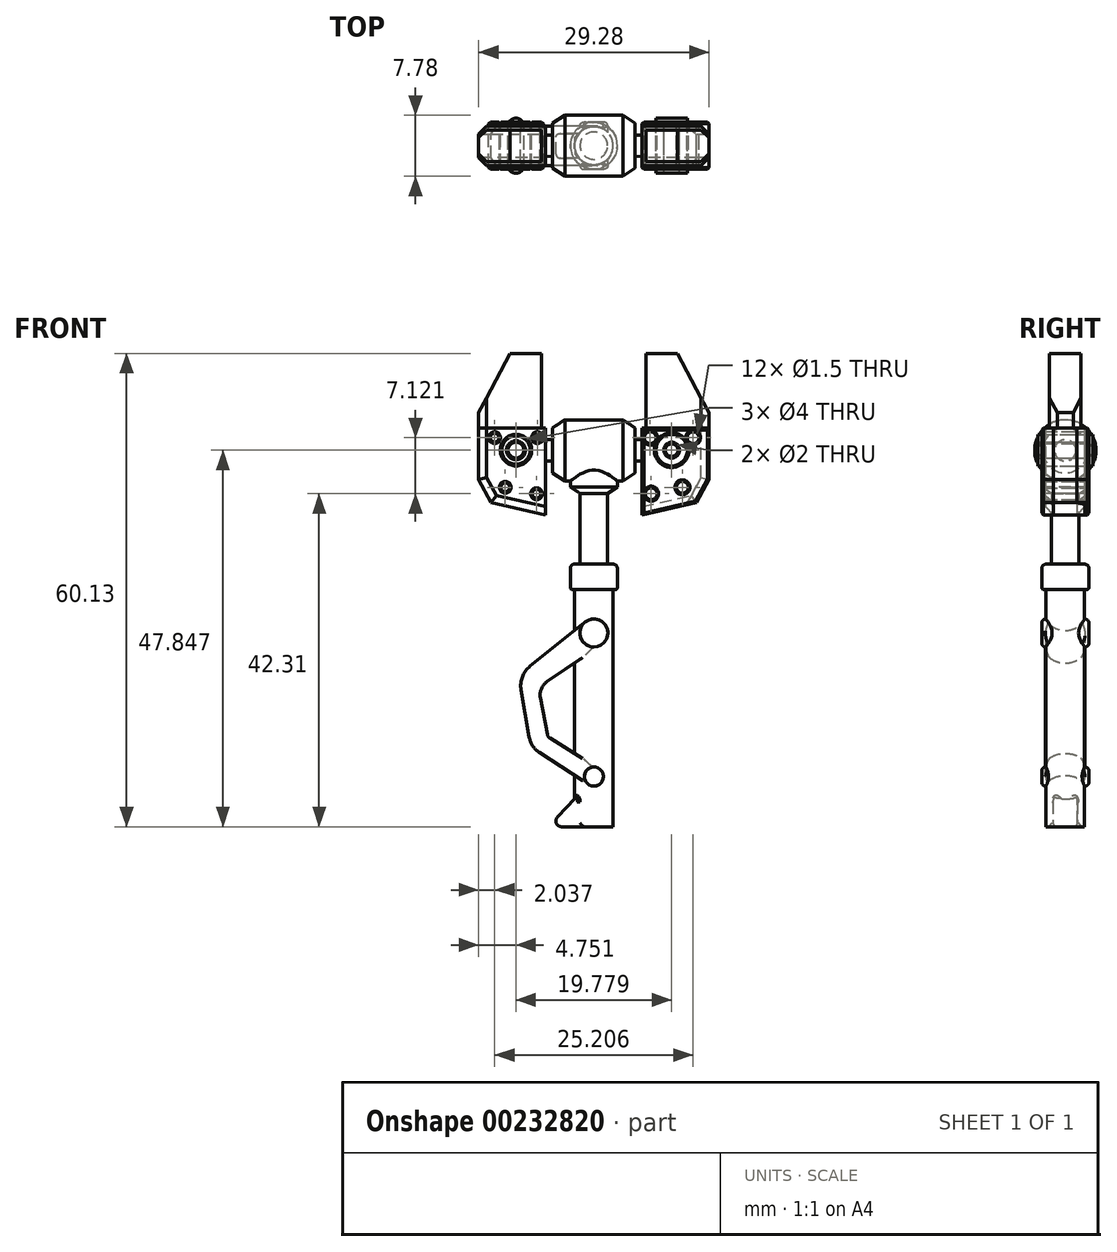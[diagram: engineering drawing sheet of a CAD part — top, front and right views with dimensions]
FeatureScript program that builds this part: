
annotation { "Feature Type Name" : "Feature", "Feature Type Description" : "" }
export const myFeature = defineFeature(function(context is Context, id is Id, definition is map)
    precondition{}
    {
        {
            var Q0;
            Q0=qCreatedBy(makeId("Front.planeOp"),FACE);
            var sketch = newSketch(context, id + "F0", { "sketchPlane" : qUnion([Q0])});
            skLineSegment(sketch, "E0", {"start": v(0, -35.9) * mm, "end": v(0, 32.83) * mm, "construction": true});
            skSolve(sketch);
        }
        {
            var Q0;
            Q0=qCreatedBy(makeId("Front.planeOp"),FACE);
            var sketch = newSketch(context, id + "F1", { "sketchPlane" : qUnion([Q0])});
            skLineSegment(sketch, "E1", {"start": v(-6.64, 28.64) * mm, "end": v(-10.64, 28.64) * mm});
            skLineSegment(sketch, "E2", {"start": v(-10.64, 28.64) * mm, "end": v(-14.64, 21.12) * mm});
            skLineSegment(sketch, "E3", {"start": v(-14.64, 21.12) * mm, "end": v(-14.64, 12.62) * mm});
            skLineSegment(sketch, "E4", {"start": v(-14.64, 12.62) * mm, "end": v(-13.04, 9.73) * mm});
            skLineSegment(sketch, "E5", {"start": v(-13.04, 9.73) * mm, "end": v(-6.14, 8.14) * mm});
            skLineSegment(sketch, "E6", {"start": v(-6.14, 8.14) * mm, "end": v(-6.14, 19.14) * mm});
            skLineSegment(sketch, "E7", {"start": v(-6.14, 19.14) * mm, "end": v(-6.64, 19.14) * mm});
            skLineSegment(sketch, "E8", {"start": v(-6.64, 19.14) * mm, "end": v(-6.64, 28.64) * mm});
            skLineSegment(sketch, "E9", {"start": v(-6.64, 19.14) * mm, "end": v(-14.64, 19.14) * mm});
            skCircle(sketch, "E10", {"center": v(-9.89, 16.36) * mm, "radius": 1 * mm});
            skCircle(sketch, "E11.0", {"center": v(-9.89, 16.36) * mm, "radius": 2 * mm});
            skCircle(sketch, "E12", {"center": v(-11.25, 11.63) * mm, "radius": 0.75 * mm});
            skCircle(sketch, "E13", {"center": v(-7.28, 10.82) * mm, "radius": 0.75 * mm});
            skCircle(sketch, "E14", {"center": v(-7.16, 17.94) * mm, "radius": 0.75 * mm});
            skLineSegment(sketch, "E15", {"start": v(-6.14, 17.67) * mm, "end": v(-5.23, 17.68) * mm});
            skLineSegment(sketch, "E16", {"start": v(-5.23, 17.68) * mm, "end": v(-5.25, 19.18) * mm});
            skLineSegment(sketch, "E17", {"start": v(-5.25, 19.18) * mm, "end": v(-3.69, 20.2) * mm});
            skLineSegment(sketch, "E18", {"start": v(-6.14, 16.32) * mm, "end": v(0, 16.32) * mm});
            skLineSegment(sketch, "E19.MirrorCS", {"start": v(6.14, 16.32) * mm, "end": v(0, 16.32) * mm});
            skLineSegment(sketch, "E20.MirrorCS", {"start": v(6.64, 19.14) * mm, "end": v(6.64, 28.64) * mm});
            skLineSegment(sketch, "E21.MirrorCS", {"start": v(6.64, 28.64) * mm, "end": v(10.64, 28.64) * mm});
            skLineSegment(sketch, "E22.MirrorCS", {"start": v(10.64, 28.64) * mm, "end": v(14.64, 21.12) * mm});
            skLineSegment(sketch, "E23.MirrorCS", {"start": v(6.64, 19.14) * mm, "end": v(14.64, 19.14) * mm});
            skLineSegment(sketch, "E24.MirrorCS", {"start": v(6.14, 8.14) * mm, "end": v(6.14, 19.14) * mm});
            skLineSegment(sketch, "E25.MirrorCS", {"start": v(13.04, 9.73) * mm, "end": v(6.14, 8.14) * mm});
            skLineSegment(sketch, "E26.MirrorCS", {"start": v(14.64, 12.62) * mm, "end": v(13.04, 9.73) * mm});
            skLineSegment(sketch, "E27.MirrorCS", {"start": v(14.64, 21.12) * mm, "end": v(14.64, 12.62) * mm});
            skLineSegment(sketch, "E28.MirrorCS", {"start": v(6.14, 19.14) * mm, "end": v(6.64, 19.14) * mm});
            skCircle(sketch, "E29.MirrorC", {"center": v(7.16, 17.94) * mm, "radius": 0.75 * mm});
            skCircle(sketch, "E30.MirrorC", {"center": v(9.89, 16.36) * mm, "radius": 1 * mm});
            skCircle(sketch, "E31.MirrorC", {"center": v(9.89, 16.36) * mm, "radius": 2 * mm});
            skCircle(sketch, "E32.MirrorC", {"center": v(11.25, 11.63) * mm, "radius": 0.75 * mm});
            skCircle(sketch, "E33.MirrorC", {"center": v(7.28, 10.82) * mm, "radius": 0.75 * mm});
            skCircle(sketch, "E34", {"center": v(-12.6, 17.94) * mm, "radius": 0.75 * mm});
            skCircle(sketch, "E35.MirrorC", {"center": v(12.6, 17.94) * mm, "radius": 0.75 * mm});
            skLineSegment(sketch, "E36", {"start": v(-3.69, 20.2) * mm, "end": v(0, 20.2) * mm});
            skLineSegment(sketch, "E37.MirrorCS", {"start": v(3.69, 20.2) * mm, "end": v(0, 20.2) * mm});
            skLineSegment(sketch, "E38.MirrorCS", {"start": v(5.25, 19.18) * mm, "end": v(3.69, 20.2) * mm});
            skLineSegment(sketch, "E39.MirrorCS", {"start": v(5.23, 17.68) * mm, "end": v(5.25, 19.18) * mm});
            skLineSegment(sketch, "E40.MirrorCS", {"start": v(6.14, 17.67) * mm, "end": v(5.23, 17.68) * mm});
            skSolve(sketch);
        }
        {
            var Q0;
            {var subQ4=sQuery(id+"F1.wireOp",EDGE,"E15");Q0=makeQuery(id+"F1.imprint","IMPRINT",FACE,{"disambiguationData":[TD([[makeQuery(id+"F1.imprint","IMPRINT",EDGE,{"derivedFrom":subQ4}),-1.0]])]});}
            var Q1;
            Q1=makeQuery(id+"F1.imprint","IMPRINT",FACE,{"disambiguationData":[TD([[makeQuery(id+"F1.imprint","IMPRINT",EDGE,{"derivedFrom":sQuery(id+"F1.wireOp",EDGE,"R4rRVu6B-g3JG-Hnan-cle3-3YQuGjeQOPrk")}),-1.0]])]});
            var Q2;
            Q2=makeQuery(id+"F1.imprint","IMPRINT",FACE,{"disambiguationData":[TD([[makeQuery(id+"F1.imprint","IMPRINT",EDGE,{"derivedFrom":sQuery(id+"F1.wireOp",EDGE,"RKqnByiM-5ZUj-5foz-eMzT-fc1n69alfR5G")}),-1.0]])]});
            var Q3;
            {var subQ0=sQuery(id+"F1.wireOp",EDGE,"f581a503-3708-428f-8b60-acb21600f56f0.MirrorCS");Q3=makeQuery(id+"F1.imprint","IMPRINT",FACE,{"disambiguationData":[TD([[makeQuery(id+"F1.imprint","IMPRINT",EDGE,{"derivedFrom":subQ0}),1.0]])]});}
            var Q4;
            {var subQ1=sQuery(id+"F1.wireOp",EDGE,"bd6f6f71-7a97-47fd-9cc7-a4106de6fa7d0.MirrorCS");Q4=makeQuery(id+"F1.imprint","IMPRINT",FACE,{"disambiguationData":[TD([[makeQuery(id+"F1.imprint","IMPRINT",EDGE,{"derivedFrom":subQ1}),1.0]])]});}
            var Q5;
            Q5=sQuery(id+"F1.wireOp",EDGE,"E18");
            revolve(context, id + "F2", {"entities" : qUnion([Q0, Q1, Q2, Q3, Q4]), "axis" : qUnion([Q5]), "revolveType" : RevolveType.FULL});
        }
        {
            var Q0;
            Q0=makeQuery(id+"F1.imprint","IMPRINT",FACE,{"disambiguationData":[TD([[makeQuery(id+"F1.imprint","IMPRINT",EDGE,{"derivedFrom":sQuery(id+"F1.wireOp",EDGE,"E1")}),1.0]])]});
            var Q1;
            Q1=makeQuery(id+"F1.imprint","IMPRINT",FACE,{"disambiguationData":[TD([[makeQuery(id+"F1.imprint","IMPRINT",EDGE,{"derivedFrom":sQuery(id+"F1.wireOp",EDGE,"E20.MirrorCS")}),-1.0]])]});
            extrude(context, id + "F3", {"entities" : qUnion([Q0, Q1]), "endBound" : BoundingType.SYMMETRIC, "depth" : 4 * mm});
        }
        {
            var Q0;
            {var subQ5=sQuery(id+"F1.wireOp",EDGE,"E4");Q0=makeQuery(id+"F1.imprint","IMPRINT",FACE,{"disambiguationData":[TD([[makeQuery(id+"F1.imprint","IMPRINT",EDGE,{"derivedFrom":subQ5}),1.0]])]});}
            var Q1;
            {var subQ2=sQuery(id+"F1.wireOp",EDGE,"E23.MirrorCS");Q1=makeQuery(id+"F1.imprint","IMPRINT",FACE,{"disambiguationData":[TD([[makeQuery(id+"F1.imprint","IMPRINT",EDGE,{"derivedFrom":subQ2}),-1.0]])]});}
            extrude(context, id + "F4", {"entities" : qUnion([Q0, Q1]), "endBound" : BoundingType.SYMMETRIC, "depth" : 5 * mm});
        }
        {
            var Q0;
            Q0=makeQuery(id+"F1.imprint","IMPRINT",FACE,{"disambiguationData":[TD([[makeQuery(id+"F1.imprint","IMPRINT",EDGE,{"derivedFrom":sQuery(id+"F1.wireOp",EDGE,"E13")}),1.0]])]});
            var Q1;
            Q1=makeQuery(id+"F1.imprint","IMPRINT",FACE,{"disambiguationData":[TD([[makeQuery(id+"F1.imprint","IMPRINT",EDGE,{"derivedFrom":sQuery(id+"F1.wireOp",EDGE,"E12")}),1.0]])]});
            var Q2;
            Q2=makeQuery(id+"F1.imprint","IMPRINT",FACE,{"disambiguationData":[TD([[makeQuery(id+"F1.imprint","IMPRINT",EDGE,{"derivedFrom":sQuery(id+"F1.wireOp",EDGE,"E34")}),1.0]])]});
            var Q3;
            Q3=makeQuery(id+"F1.imprint","IMPRINT",FACE,{"disambiguationData":[TD([[makeQuery(id+"F1.imprint","IMPRINT",EDGE,{"derivedFrom":sQuery(id+"F1.wireOp",EDGE,"E14")}),1.0]])]});
            var Q4;
            Q4=makeQuery(id+"F1.imprint","IMPRINT",FACE,{"disambiguationData":[TD([[makeQuery(id+"F1.imprint","IMPRINT",EDGE,{"derivedFrom":sQuery(id+"F1.wireOp",EDGE,"E29.MirrorC")}),-1.0]])]});
            var Q5;
            Q5=makeQuery(id+"F1.imprint","IMPRINT",FACE,{"disambiguationData":[TD([[makeQuery(id+"F1.imprint","IMPRINT",EDGE,{"derivedFrom":sQuery(id+"F1.wireOp",EDGE,"E33.MirrorC")}),-1.0]])]});
            var Q6;
            Q6=makeQuery(id+"F1.imprint","IMPRINT",FACE,{"disambiguationData":[TD([[makeQuery(id+"F1.imprint","IMPRINT",EDGE,{"derivedFrom":sQuery(id+"F1.wireOp",EDGE,"E32.MirrorC")}),-1.0]])]});
            var Q7;
            Q7=makeQuery(id+"F1.imprint","IMPRINT",FACE,{"disambiguationData":[TD([[makeQuery(id+"F1.imprint","IMPRINT",EDGE,{"derivedFrom":sQuery(id+"F1.wireOp",EDGE,"E35.MirrorC")}),-1.0]])]});
            var Q8;
            Q8=makeQuery(id+"F1.imprint","IMPRINT",FACE,{"disambiguationData":[TD([[makeQuery(id+"F1.imprint","IMPRINT",EDGE,{"derivedFrom":sQuery(id+"F1.wireOp",EDGE,"E10")}),-1.0]])]});
            var Q9;
            Q9=makeQuery(id+"F1.imprint","IMPRINT",FACE,{"disambiguationData":[TD([[makeQuery(id+"F1.imprint","IMPRINT",EDGE,{"derivedFrom":sQuery(id+"F1.wireOp",EDGE,"E30.MirrorC")}),1.0]])]});
            extrude(context, id + "F5", {"entities" : qUnion([Q0, Q1, Q2, Q3, Q4, Q5, Q6, Q7, Q8, Q9]), "endBound" : BoundingType.SYMMETRIC, "depth" : 6 * mm});
        }
        {
            var Q0;
            Q0=makeQuery(id+"F1.imprint","IMPRINT",FACE,{"disambiguationData":[TD([[makeQuery(id+"F1.imprint","IMPRINT",EDGE,{"derivedFrom":sQuery(id+"F1.wireOp",EDGE,"E10")}),1.0]])]});
            var Q1;
            Q1=makeQuery(id+"F1.imprint","IMPRINT",FACE,{"disambiguationData":[TD([[makeQuery(id+"F1.imprint","IMPRINT",EDGE,{"derivedFrom":sQuery(id+"F1.wireOp",EDGE,"E30.MirrorC")}),-1.0]])]});
            extrude(context, id + "F6", {"entities" : qUnion([Q0, Q1]), "endBound" : BoundingType.SYMMETRIC, "depth" : 7 * mm});
        }
        {
            var Q0;
            Q0=makeQuery(id+"F4.opExtrude","CAP_EDGE",EDGE,{"disambiguationData":[OSD([sQuery(id+"F1.wireOp",EDGE,"E3")])],"isStart":false});
            var Q1;
            Q1=makeQuery(id+"F4.opExtrude","CAP_EDGE",EDGE,{"disambiguationData":[OSD([sQuery(id+"F1.wireOp",EDGE,"E4")])],"isStart":false});
            var Q2;
            Q2=makeQuery(id+"F4.opExtrude","CAP_EDGE",EDGE,{"disambiguationData":[OSD([sQuery(id+"F1.wireOp",EDGE,"E5")])],"isStart":false});
            var Q3;
            Q3=makeQuery(id+"F3.opExtrude","CAP_EDGE",EDGE,{"disambiguationData":[OSD([sQuery(id+"F1.wireOp",EDGE,"E3")])],"isStart":false});
            var Q4;
            Q4=makeQuery(id+"F3.opExtrude","CAP_EDGE",EDGE,{"disambiguationData":[OSD([sQuery(id+"F1.wireOp",EDGE,"E3")])],"isStart":true});
            var Q5;
            Q5=makeQuery(id+"F4.opExtrude","CAP_EDGE",EDGE,{"disambiguationData":[OSD([sQuery(id+"F1.wireOp",EDGE,"E3")])],"isStart":true});
            var Q6;
            Q6=makeQuery(id+"F4.opExtrude","CAP_EDGE",EDGE,{"disambiguationData":[OSD([sQuery(id+"F1.wireOp",EDGE,"E4")])],"isStart":true});
            var Q7;
            Q7=makeQuery(id+"F4.opExtrude","CAP_EDGE",EDGE,{"disambiguationData":[OSD([sQuery(id+"F1.wireOp",EDGE,"E5")])],"isStart":true});
            var Q8;
            Q8=makeQuery(id+"F3.opExtrude","CAP_EDGE",EDGE,{"disambiguationData":[OSD([sQuery(id+"F1.wireOp",EDGE,"E27.MirrorCS")])],"isStart":false});
            var Q9;
            Q9=makeQuery(id+"F4.opExtrude","CAP_EDGE",EDGE,{"disambiguationData":[OSD([sQuery(id+"F1.wireOp",EDGE,"E27.MirrorCS")])],"isStart":false});
            var Q10;
            Q10=makeQuery(id+"F4.opExtrude","CAP_EDGE",EDGE,{"disambiguationData":[OSD([sQuery(id+"F1.wireOp",EDGE,"E26.MirrorCS")])],"isStart":false});
            var Q11;
            Q11=makeQuery(id+"F4.opExtrude","CAP_EDGE",EDGE,{"disambiguationData":[OSD([sQuery(id+"F1.wireOp",EDGE,"E25.MirrorCS")])],"isStart":false});
            var Q12;
            Q12=makeQuery(id+"F3.opExtrude","CAP_EDGE",EDGE,{"disambiguationData":[OSD([sQuery(id+"F1.wireOp",EDGE,"E27.MirrorCS")])],"isStart":true});
            var Q13;
            Q13=makeQuery(id+"F4.opExtrude","CAP_EDGE",EDGE,{"disambiguationData":[OSD([sQuery(id+"F1.wireOp",EDGE,"E27.MirrorCS")])],"isStart":true});
            var Q14;
            Q14=makeQuery(id+"F4.opExtrude","CAP_EDGE",EDGE,{"disambiguationData":[OSD([sQuery(id+"F1.wireOp",EDGE,"E26.MirrorCS")])],"isStart":true});
            chamfer(context, id + "F7", {"entities" : qUnion([Q0, Q1, Q2, Q3, Q4, Q5, Q6, Q7, Q8, Q9, Q10, Q11, Q12, Q13, Q14]), "width" : 1 * mm, "tangentPropagation" : true});
        }
        {
            var Q0;
            Q0=makeQuery(id+"F6.opExtrude","CAP_FACE",FACE,{"disambiguationData":[OSD([sQuery(id+"F1.wireOp",EDGE,"E10")])],"isStart":false});
            var Q1;
            Q1=makeQuery(id+"F6.opExtrude","CAP_FACE",FACE,{"disambiguationData":[OSD([sQuery(id+"F1.wireOp",EDGE,"E30.MirrorC")])],"isStart":false});
            var Q2;
            Q2=makeQuery(id+"F6.opExtrude","CAP_FACE",FACE,{"disambiguationData":[OSD([sQuery(id+"F1.wireOp",EDGE,"E30.MirrorC")])],"isStart":true});
            var Q3;
            Q3=makeQuery(id+"F6.opExtrude","CAP_FACE",FACE,{"disambiguationData":[OSD([sQuery(id+"F1.wireOp",EDGE,"E10")])],"isStart":true});
            fillet(context, id + "F8", {"entities" : qUnion([Q0, Q1, Q2, Q3]), "radius" : 1 * mm, "tangentPropagation" : true, "allowEdgeOverflow" : false});
        }
        {
            var Q0;
            Q0=makeQuery(id+"F5.opExtrude","CAP_FACE",FACE,{"disambiguationData":[OSD([sQuery(id+"F1.wireOp",EDGE,"E34")])],"isStart":false});
            var Q1;
            Q1=makeQuery(id+"F5.opExtrude","CAP_FACE",FACE,{"disambiguationData":[OSD([sQuery(id+"F1.wireOp",EDGE,"E14")])],"isStart":false});
            var Q2;
            Q2=makeQuery(id+"F5.opExtrude","CAP_FACE",FACE,{"disambiguationData":[OSD([sQuery(id+"F1.wireOp",EDGE,"E10"),sQuery(id+"F1.wireOp",EDGE,"E11.0")])],"isStart":false});
            var Q3;
            Q3=makeQuery(id+"F5.opExtrude","CAP_FACE",FACE,{"disambiguationData":[OSD([sQuery(id+"F1.wireOp",EDGE,"E13")])],"isStart":false});
            var Q4;
            Q4=makeQuery(id+"F5.opExtrude","CAP_FACE",FACE,{"disambiguationData":[OSD([sQuery(id+"F1.wireOp",EDGE,"E12")])],"isStart":false});
            var Q5;
            Q5=makeQuery(id+"F5.opExtrude","CAP_FACE",FACE,{"disambiguationData":[OSD([sQuery(id+"F1.wireOp",EDGE,"E29.MirrorC")])],"isStart":false});
            var Q6;
            Q6=makeQuery(id+"F5.opExtrude","CAP_FACE",FACE,{"disambiguationData":[OSD([sQuery(id+"F1.wireOp",EDGE,"E35.MirrorC")])],"isStart":false});
            var Q7;
            Q7=makeQuery(id+"F5.opExtrude","CAP_FACE",FACE,{"disambiguationData":[OSD([sQuery(id+"F1.wireOp",EDGE,"E32.MirrorC")])],"isStart":false});
            var Q8;
            Q8=makeQuery(id+"F5.opExtrude","CAP_FACE",FACE,{"disambiguationData":[OSD([sQuery(id+"F1.wireOp",EDGE,"E33.MirrorC")])],"isStart":false});
            var Q9;
            Q9=makeQuery(id+"F5.opExtrude","CAP_FACE",FACE,{"disambiguationData":[OSD([sQuery(id+"F1.wireOp",EDGE,"E35.MirrorC")])],"isStart":true});
            var Q10;
            Q10=makeQuery(id+"F5.opExtrude","CAP_FACE",FACE,{"disambiguationData":[OSD([sQuery(id+"F1.wireOp",EDGE,"E29.MirrorC")])],"isStart":true});
            var Q11;
            Q11=makeQuery(id+"F5.opExtrude","CAP_FACE",FACE,{"disambiguationData":[OSD([sQuery(id+"F1.wireOp",EDGE,"E33.MirrorC")])],"isStart":true});
            var Q12;
            Q12=makeQuery(id+"F5.opExtrude","CAP_FACE",FACE,{"disambiguationData":[OSD([sQuery(id+"F1.wireOp",EDGE,"E32.MirrorC")])],"isStart":true});
            var Q13;
            Q13=makeQuery(id+"F5.opExtrude","CAP_FACE",FACE,{"disambiguationData":[OSD([sQuery(id+"F1.wireOp",EDGE,"E30.MirrorC"),sQuery(id+"F1.wireOp",EDGE,"E31.MirrorC")])],"isStart":true});
            var Q14;
            Q14=makeQuery(id+"F5.opExtrude","CAP_FACE",FACE,{"disambiguationData":[OSD([sQuery(id+"F1.wireOp",EDGE,"E10"),sQuery(id+"F1.wireOp",EDGE,"E11.0")])],"isStart":true});
            var Q15;
            Q15=makeQuery(id+"F5.opExtrude","CAP_FACE",FACE,{"disambiguationData":[OSD([sQuery(id+"F1.wireOp",EDGE,"E14")])],"isStart":true});
            var Q16;
            Q16=makeQuery(id+"F5.opExtrude","CAP_EDGE",EDGE,{"disambiguationData":[OSD([sQuery(id+"F1.wireOp",EDGE,"E34")])],"isStart":true});
            var Q17;
            Q17=makeQuery(id+"F5.opExtrude","CAP_FACE",FACE,{"disambiguationData":[OSD([sQuery(id+"F1.wireOp",EDGE,"E12")])],"isStart":true});
            var Q18;
            Q18=makeQuery(id+"F5.opExtrude","CAP_FACE",FACE,{"disambiguationData":[OSD([sQuery(id+"F1.wireOp",EDGE,"E13")])],"isStart":true});
            var Q19;
            Q19=makeQuery(id+"F5.opExtrude","CAP_FACE",FACE,{"disambiguationData":[OSD([sQuery(id+"F1.wireOp",EDGE,"E30.MirrorC"),sQuery(id+"F1.wireOp",EDGE,"E31.MirrorC")])],"isStart":false});
            chamfer(context, id + "F9", {"entities" : qUnion([Q0, Q1, Q2, Q3, Q4, Q5, Q6, Q7, Q8, Q9, Q10, Q11, Q12, Q13, Q14, Q15, Q16, Q17, Q18, Q19]), "width" : .2 * mm, "tangentPropagation" : true});
        }
        {
            var Q0;
            Q0=qCreatedBy(makeId("Front.planeOp"),FACE);
            var sketch = newSketch(context, id + "F10", { "sketchPlane" : qUnion([Q0])});
            skLineSegment(sketch, "E41", {"start": v(-2.99, 14.09) * mm, "end": v(-2.99, 11.69) * mm});
            skLineSegment(sketch, "E42", {"start": v(-2.99, 11.69) * mm, "end": v(-1.75, 10.85) * mm});
            skLineSegment(sketch, "E43", {"start": v(-1.75, 10.85) * mm, "end": v(-1.75, 1.88) * mm});
            skLineSegment(sketch, "E44", {"start": v(-1.75, 1.88) * mm, "end": v(-2.44, 1.88) * mm});
            skLineSegment(sketch, "E45", {"start": v(-2.99, 1.33) * mm, "end": v(-2.99, -1.1) * mm});
            skLineSegment(sketch, "E46", {"start": v(-2.73, -1.36) * mm, "end": v(-2.45, -1.36) * mm});
            skLineSegment(sketch, "E47", {"start": v(-2.45, -1.36) * mm, "end": v(-2.45, -31.49) * mm});
            skLineSegment(sketch, "E48", {"start": v(-2.45, -31.49) * mm, "end": v(0, -31.49) * mm});
            skPoint(sketch, "E49.visualSharp", {"position": v(-2.99, 1.88) * mm});
            skArc(sketch, "E49.filletArc", {"start": v(-2.44, 1.88) * mm, "mid": v(-2.83, 1.72) * mm, "end": v(-2.99, 1.33) * mm});
            skPoint(sketch, "E50.visualSharp", {"position": v(-2.99, -1.36) * mm});
            skArc(sketch, "E50.filletArc", {"start": v(-2.99, -1.1) * mm, "mid": v(-2.91, -1.28) * mm, "end": v(-2.73, -1.36) * mm});
            skLineSegment(sketch, "E51", {"start": v(0, -31.49) * mm, "end": v(0, 14.09) * mm});
            skLineSegment(sketch, "E52", {"start": v(0, 14.09) * mm, "end": v(-2.99, 14.09) * mm});
            skSolve(sketch);
        }
        {
            var Q0;
            Q0=makeQuery(id+"F10.imprint","IMPRINT",FACE,{"disambiguationData":[TD([[makeQuery(id+"F10.imprint","IMPRINT",EDGE,{"derivedFrom":sQuery(id+"F10.wireOp",EDGE,"E41")}),1.0]])]});
            var Q1;
            Q1=sQuery(id+"F0.wireOp",EDGE,"E0");
            revolve(context, id + "F11", {"operationType" : NewBodyOperationType.ADD, "entities" : qUnion([Q0]), "axis" : qUnion([Q1]), "revolveType" : RevolveType.FULL});
        }
        {
            var Q0;
            Q0=qCreatedBy(makeId("Front.planeOp"),FACE);
            var sketch = newSketch(context, id + "F12", { "sketchPlane" : qUnion([Q0])});
            skCircle(sketch, "E53", {"center": v(0, -25.1) * mm, "radius": 1.21 * mm});
            skCircle(sketch, "E54", {"center": v(0, -6.87) * mm, "radius": 1.78 * mm});
            skLineSegment(sketch, "E55", {"start": v(-1.11, -5.49) * mm, "end": v(-8.1, -11.08) * mm});
            skLineSegment(sketch, "E56", {"start": v(-0.66, -26.12) * mm, "end": v(-6.9, -22.07) * mm});
            skLineSegment(sketch, "E57", {"start": v(-9.24, -14.13) * mm, "end": v(-8.2, -20.1) * mm});
            skLineSegment(sketch, "E58", {"start": v(1, -8.34) * mm, "end": v(-5.94, -13.06) * mm});
            skLineSegment(sketch, "E59", {"start": v(-6.79, -15.1) * mm, "end": v(-5.9, -19.75) * mm});
            skLineSegment(sketch, "E60", {"start": v(0.64, -24.08) * mm, "end": v(-5.58, -20.23) * mm});
            skPoint(sketch, "E61.visualSharp", {"position": v(-9.57, -12.27) * mm});
            skArc(sketch, "E61.filletArc", {"start": v(-8.1, -11.08) * mm, "mid": v(-9.09, -12.45) * mm, "end": v(-9.24, -14.13) * mm});
            skPoint(sketch, "E62.visualSharp", {"position": v(-7.98, -21.36) * mm});
            skArc(sketch, "E62.filletArc", {"start": v(-8.2, -20.1) * mm, "mid": v(-7.76, -21.22) * mm, "end": v(-6.9, -22.07) * mm});
            skPoint(sketch, "E63.visualSharp", {"position": v(-5.85, -20.06) * mm});
            skArc(sketch, "E63.filletArc", {"start": v(-5.9, -19.75) * mm, "mid": v(-5.8, -20.02) * mm, "end": v(-5.58, -20.23) * mm});
            skPoint(sketch, "E64.visualSharp", {"position": v(-7.03, -13.8) * mm});
            skArc(sketch, "E64.filletArc", {"start": v(-5.94, -13.06) * mm, "mid": v(-6.67, -13.95) * mm, "end": v(-6.79, -15.1) * mm});
            skLineSegment(sketch, "E65", {"start": v(-2.45, -31.48) * mm, "end": v(-2.45, -1.36) * mm});
            skLineSegment(sketch, "E66.0", {"start": v(2.45, -31.49) * mm, "end": v(-2.45, -31.49) * mm});
            skLineSegment(sketch, "E67", {"start": v(-1.88, -27.38) * mm, "end": v(-4.62, -30.27) * mm});
            skLineSegment(sketch, "E68", {"start": v(-4.1, -31.48) * mm, "end": v(-2.45, -31.49) * mm});
            skLineSegment(sketch, "E69", {"start": v(-1.88, -27.38) * mm, "end": v(-1.88, -31.49) * mm});
            skLineSegment(sketch, "E70", {"start": v(-1.88, -31.49) * mm, "end": v(-2.45, -31.48) * mm});
            skPoint(sketch, "E71.visualSharp", {"position": v(-5.76, -31.48) * mm});
            skArc(sketch, "E71.filletArc", {"start": v(-4.62, -30.27) * mm, "mid": v(-4.76, -31.05) * mm, "end": v(-4.1, -31.48) * mm});
            skSolve(sketch);
        }
        {
            var Q0;
            {var subQ0=sQuery(id+"F12.wireOp",EDGE,"E53");var subQ1=makeQuery(id+"F12.imprint","INTERSECT",VERTEX,{"derivedFrom":[subQ0,sQuery(id+"F12.wireOp",EDGE,"E56")]});Q0=makeQuery(id+"F12.imprint","IMPRINT",FACE,{"disambiguationData":[TD([[makeQuery(id+"F12.imprint","IMPRINT",EDGE,{"disambiguationData":[TD([[subQ1,1.0]])],"derivedFrom":subQ0}),1.0]])]});}
            var Q1;
            {var subQ0=sQuery(id+"F12.wireOp",EDGE,"E54");var subQ1=makeQuery(id+"F12.imprint","INTERSECT",VERTEX,{"derivedFrom":[subQ0,sQuery(id+"F12.wireOp",EDGE,"E55")]});Q1=makeQuery(id+"F12.imprint","IMPRINT",FACE,{"disambiguationData":[TD([[makeQuery(id+"F12.imprint","IMPRINT",EDGE,{"disambiguationData":[TD([[subQ1,-1.0]])],"derivedFrom":subQ0}),1.0]])]});}
            extrude(context, id + "F13", {"entities" : qUnion([Q0, Q1]), "operationType" : NewBodyOperationType.ADD, "endBound" : BoundingType.SYMMETRIC, "depth" : 6 * mm});
        }
        {
            var Q0;
            {var subQ1=sQuery(id+"F12.wireOp",EDGE,"E55");Q0=makeQuery(id+"F12.imprint","IMPRINT",FACE,{"disambiguationData":[TD([[makeQuery(id+"F12.imprint","IMPRINT",EDGE,{"derivedFrom":subQ1}),1.0]])]});}
            var Q1;
            Q1=makeQuery(id+"F12.imprint","IMPRINT",FACE,{"disambiguationData":[TD([[makeQuery(id+"F12.imprint","IMPRINT",EDGE,{"derivedFrom":sQuery(id+"F12.wireOp",EDGE,"E57")}),1.0]])]});
            var Q2;
            {var subQ0=sQuery(id+"F12.wireOp",EDGE,"E56");var subQ1=sQuery(id+"F12.wireOp",EDGE,"E53");var subQ2=makeQuery(id+"F12.imprint","INTERSECT",VERTEX,{"derivedFrom":[subQ1,subQ0]});Q2=makeQuery(id+"F12.imprint","IMPRINT",FACE,{"disambiguationData":[TD([[makeQuery(id+"F12.imprint","IMPRINT",EDGE,{"disambiguationData":[TD([[subQ2,1.0]])],"derivedFrom":subQ1}),-1.0]])]});}
            extrude(context, id + "F14", {"entities" : qUnion([Q0, Q1, Q2]), "operationType" : NewBodyOperationType.ADD, "endBound" : BoundingType.SYMMETRIC, "depth" : 5 * mm});
        }
        {
            var Q0;
            Q0=makeQuery(id+"F13.opExtrude","CAP_FACE",FACE,{"disambiguationData":[OSD([sQuery(id+"F12.wireOp",EDGE,"E54")])],"isStart":false});
            var Q1;
            Q1=makeQuery(id+"F13.opExtrude","CAP_FACE",FACE,{"disambiguationData":[OSD([sQuery(id+"F12.wireOp",EDGE,"E54")])],"isStart":true});
            var Q2;
            Q2=makeQuery(id+"F13.opExtrude","CAP_FACE",FACE,{"disambiguationData":[OSD([sQuery(id+"F12.wireOp",EDGE,"E53")])],"isStart":true});
            var Q3;
            Q3=makeQuery(id+"F13.opExtrude","CAP_FACE",FACE,{"disambiguationData":[OSD([sQuery(id+"F12.wireOp",EDGE,"E53")])],"isStart":false});
            fillet(context, id + "F15", {"entities" : qUnion([Q0, Q1, Q2, Q3]), "radius" : .5 * mm, "tangentPropagation" : true, "allowEdgeOverflow" : false});
        }
        {
            var Q0;
            Q0=makeQuery(id+"F14.opExtrude","CAP_EDGE",EDGE,{"disambiguationData":[OSD([sQuery(id+"F12.wireOp",EDGE,"E58")])],"isStart":false});
            var Q1;
            Q1=makeQuery(id+"F14.opExtrude","CAP_EDGE",EDGE,{"disambiguationData":[OSD([sQuery(id+"F12.wireOp",EDGE,"E57")])],"isStart":false});
            var Q2;
            Q2=makeQuery(id+"F14.opExtrude","CAP_EDGE",EDGE,{"disambiguationData":[OSD([sQuery(id+"F12.wireOp",EDGE,"E55")])],"isStart":true});
            var Q3;
            Q3=makeQuery(id+"F14.opExtrude","CAP_EDGE",EDGE,{"disambiguationData":[OSD([sQuery(id+"F12.wireOp",EDGE,"E58")])],"isStart":true});
            fillet(context, id + "F16", {"entities" : qUnion([Q0, Q1, Q2, Q3]), "radius" : .5 * mm, "tangentPropagation" : true, "allowEdgeOverflow" : false});
        }
        {
            var Q0;
            {var subQ4=sQuery(id+"F12.wireOp",EDGE,"E69");Q0=makeQuery(id+"F12.imprint","IMPRINT",FACE,{"disambiguationData":[TD([[makeQuery(id+"F12.imprint","IMPRINT",EDGE,{"derivedFrom":subQ4}),-1.0]])]});}
            var Q1;
            {var subQ4=sQuery(id+"F12.wireOp",EDGE,"E68");Q1=makeQuery(id+"F12.imprint","IMPRINT",FACE,{"disambiguationData":[TD([[makeQuery(id+"F12.imprint","IMPRINT",EDGE,{"derivedFrom":subQ4}),1.0]])]});}
            extrude(context, id + "F17", {"entities" : qUnion([Q0, Q1]), "operationType" : NewBodyOperationType.ADD, "endBound" : BoundingType.SYMMETRIC, "depth" : 3.12 * mm});
        }
        {
            var Q0;
            Q0=makeQuery(id+"F17.opExtrude","CAP_FACE",FACE,{"disambiguationData":[OSD([sQuery(id+"F12.wireOp",EDGE,"E66.0"),sQuery(id+"F12.wireOp",EDGE,"E67"),sQuery(id+"F12.wireOp",EDGE,"E68"),sQuery(id+"F12.wireOp",EDGE,"E69"),sQuery(id+"F12.wireOp",EDGE,"E71.filletArc")])],"isStart":false});
            var Q1;
            Q1=makeQuery(id+"F17.opExtrude","CAP_FACE",FACE,{"disambiguationData":[OSD([sQuery(id+"F12.wireOp",EDGE,"E66.0"),sQuery(id+"F12.wireOp",EDGE,"E67"),sQuery(id+"F12.wireOp",EDGE,"E68"),sQuery(id+"F12.wireOp",EDGE,"E69"),sQuery(id+"F12.wireOp",EDGE,"E71.filletArc")])],"isStart":true});
            fillet(context, id + "F18", {"entities" : qUnion([Q0, Q1]), "radius" : .5 * mm, "tangentPropagation" : true, "allowEdgeOverflow" : false});
        }
    });
